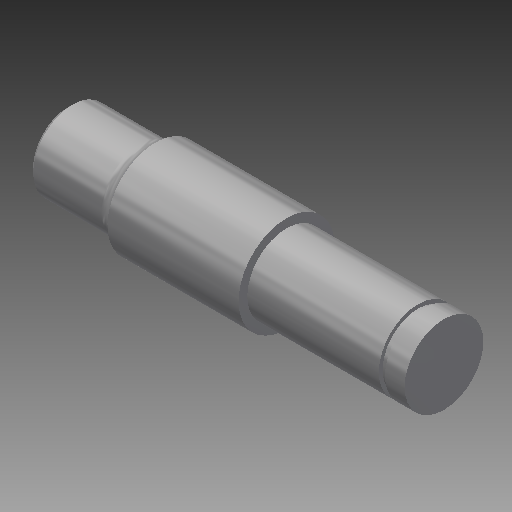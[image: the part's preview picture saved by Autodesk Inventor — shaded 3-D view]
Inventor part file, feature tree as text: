
AUTODESK INVENTOR PART (.ipt)
format: ipt  version: 2019 (Build 230136000, 136)  size: 151,552 bytes
history: native  units: mm
features: other x6, chamfer x1, fillet x1
ambient origin geometry x6: Origin, XZ Plane, XY Plane, X Axis, Y Axis, Z Axis
bodies: Body1 (feature_tree)
feature tree (8):
  other  "實體1"
  other  "迴轉1"
  chamfer  "倒角1"  [1 undecoded]
  fillet  "圓角1"  Radius=9.0mm
  other  "扣環槽1"
  other  "起始平面"
  other  "主要草圖"
  other  "iFeature27:1"
note: 1 required parameter value undecoded (feature->parameter linkage not recoverable at this tier; creation-order binding heuristic only, values carry confidence <= 0.55)
